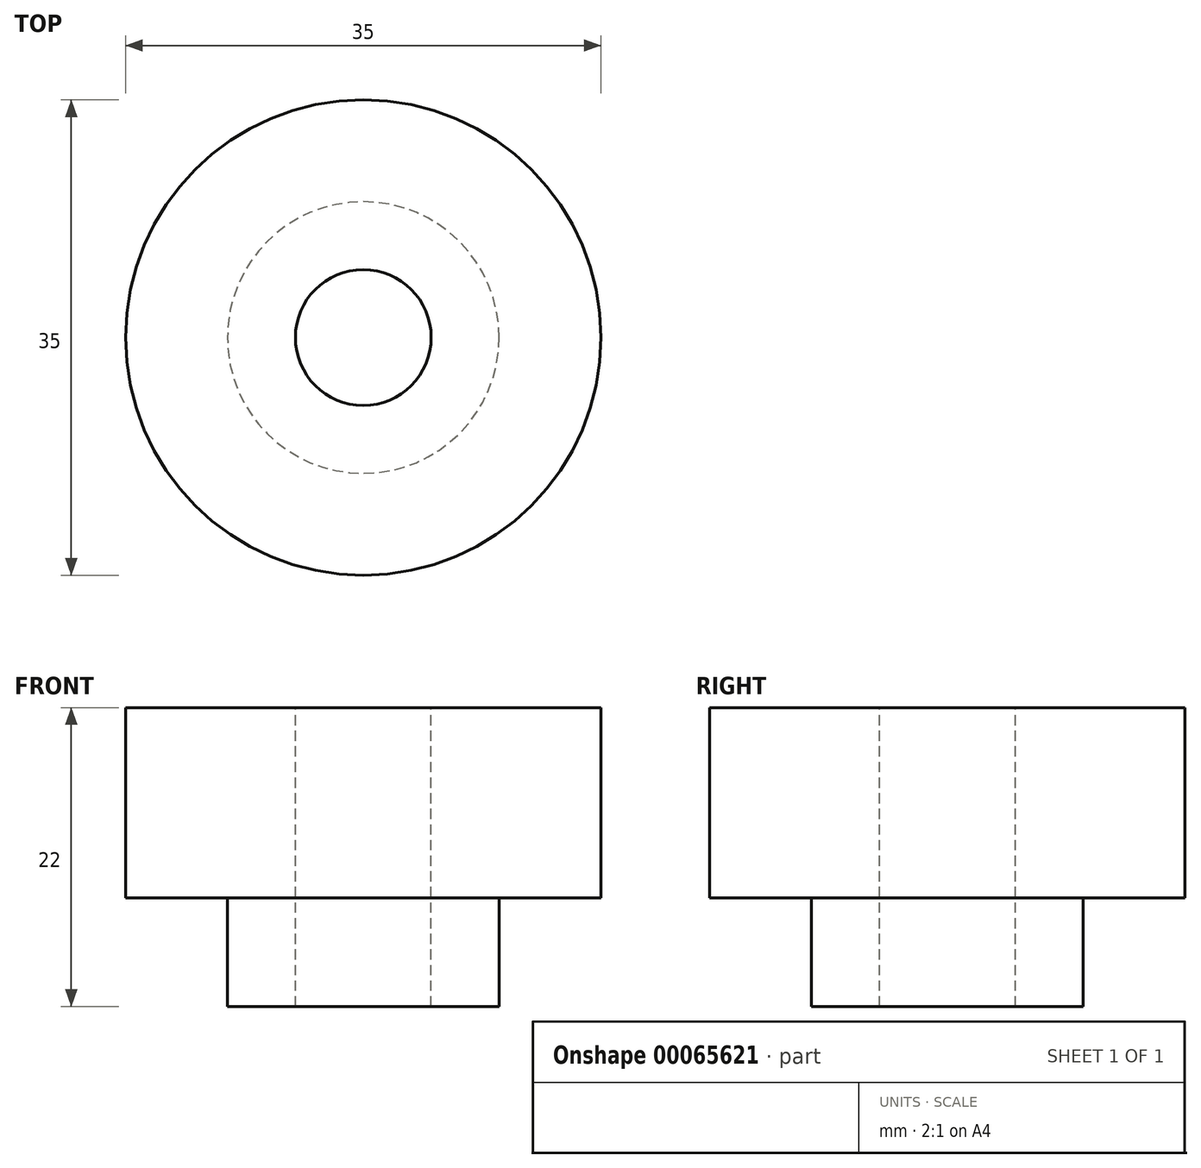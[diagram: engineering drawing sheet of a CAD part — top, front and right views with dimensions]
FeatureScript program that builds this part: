
annotation { "Feature Type Name" : "Feature", "Feature Type Description" : "" }
export const myFeature = defineFeature(function(context is Context, id is Id, definition is map)
    precondition{}
    {
        {
            var Q0;
            Q0=qCreatedBy(makeId("Top.planeOp"),FACE);
            var sketch = newSketch(context, id + "F0", { "sketchPlane" : qUnion([Q0])});
            skCircle(sketch, "E0", {"center": v(0, 0) * mm, "radius": 10 * mm});
            skSolve(sketch);
        }
        {
            var Q0;
            Q0 = qSketchRegion(id + "F0", true);
            extrude(context, id + "F1", {"entities" : qUnion([Q0]), "depth" : 8 * mm});
        }
        {
            var Q0;
            Q0=makeQuery(id+"F1.opExtrude","CAP_FACE",FACE,{"disambiguationData":[OSD([sQuery(id+"F0.wireOp",EDGE,"E0")])],"isStart":false});
            var sketch = newSketch(context, id + "F2", { "sketchPlane" : qUnion([Q0])});
            skCircle(sketch, "E1", {"center": v(0, 0) * mm, "radius": 17.5 * mm});
            skSolve(sketch);
        }
        {
            var Q0;
            Q0 = qSketchRegion(id + "F2", true);
            extrude(context, id + "F3", {"entities" : qUnion([Q0]), "operationType" : NewBodyOperationType.ADD, "depth" : 14 * mm});
        }
        {
            var Q0;
            Q0=makeQuery(id+"F3.opExtrude","CAP_FACE",FACE,{"disambiguationData":[OSD([sQuery(id+"F2.wireOp",EDGE,"E1")])],"isStart":false});
            var sketch = newSketch(context, id + "F4", { "sketchPlane" : qUnion([Q0])});
            skCircle(sketch, "E2", {"center": v(0, 0) * mm, "radius": 5 * mm});
            skSolve(sketch);
        }
        {
            var Q0;
            Q0 = qSketchRegion(id + "F4", true);
            var Q1;
            Q1=makeQuery(id+"F4.imprint","IMPRINT",FACE,{"disambiguationData":[TD([[makeQuery(id+"F4.imprint","IMPRINT",EDGE,{"derivedFrom":sQuery(id+"F4.wireOp",EDGE,"E2")}),1.0]])]});
            extrude(context, id + "F5", {"entities" : qUnion([Q0, Q1]), "operationType" : NewBodyOperationType.REMOVE, "oppositeDirection" : true, "depth" : 40 * mm});
        }
    });
